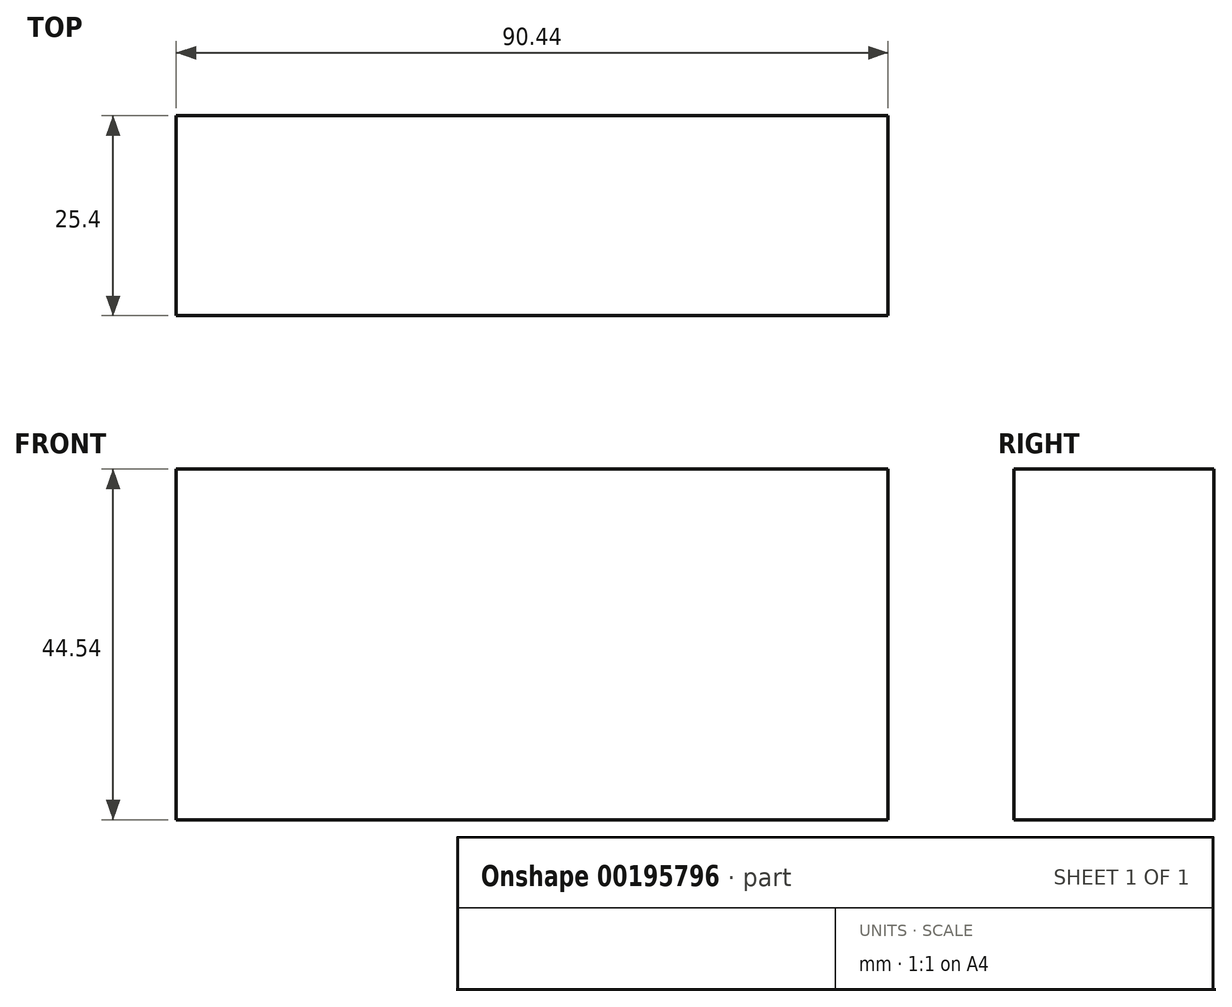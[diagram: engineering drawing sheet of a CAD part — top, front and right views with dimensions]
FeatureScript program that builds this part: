
annotation { "Feature Type Name" : "Feature", "Feature Type Description" : "" }
export const myFeature = defineFeature(function(context is Context, id is Id, definition is map)
    precondition{}
    {
        {
            var Q0;
            Q0=qCreatedBy(makeId("Front.planeOp"),FACE);
            var sketch = newSketch(context, id + "F0", { "sketchPlane" : qUnion([Q0])});
            skLineSegment(sketch, "E0.bottom", {"start": v(45.22, 22.27) * mm, "end": v(-45.22, 22.27) * mm});
            skLineSegment(sketch, "E0.top", {"start": v(45.22, -22.27) * mm, "end": v(-45.22, -22.27) * mm});
            skLineSegment(sketch, "E0.left", {"start": v(45.22, 22.27) * mm, "end": v(45.22, -22.27) * mm});
            skLineSegment(sketch, "E0.right", {"start": v(-45.22, 22.27) * mm, "end": v(-45.22, -22.27) * mm});
            skPoint(sketch, "E0.middle", {"position": v(0, 0) * mm});
            skSolve(sketch);
        }
        {
            var Q0;
            Q0 = qSketchRegion(id + "F0", true);
            extrude(context, id + "F1", {"entities" : qUnion([Q0]), "depth" : 25.4 * mm});
        }
    });
